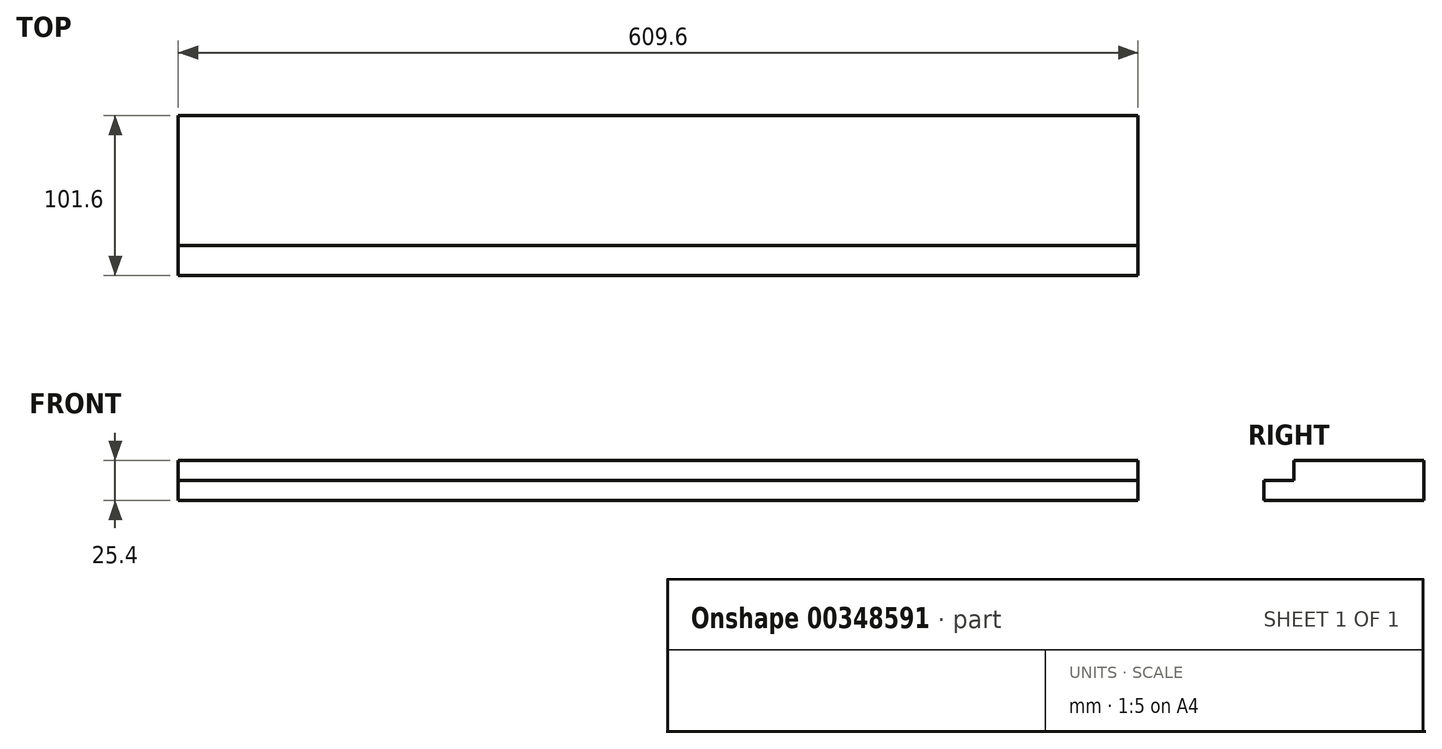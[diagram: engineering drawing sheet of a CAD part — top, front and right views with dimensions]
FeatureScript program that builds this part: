
annotation { "Feature Type Name" : "Feature", "Feature Type Description" : "" }
export const myFeature = defineFeature(function(context is Context, id is Id, definition is map)
    precondition{}
    {
        {
            var Q0;
            Q0=qCreatedBy(makeId("Top.planeOp"),FACE);
            var sketch = newSketch(context, id + "F0", { "sketchPlane" : qUnion([Q0])});
            skLineSegment(sketch, "E0.bottom", {"start": v(-308.7, 92.41) * mm, "end": v(300.9, 92.41) * mm});
            skLineSegment(sketch, "E0.top", {"start": v(-308.7, -9.19) * mm, "end": v(300.9, -9.19) * mm});
            skLineSegment(sketch, "E0.left", {"start": v(-308.7, 92.41) * mm, "end": v(-308.7, -9.19) * mm});
            skLineSegment(sketch, "E0.right", {"start": v(300.9, 92.41) * mm, "end": v(300.9, -9.19) * mm});
            skLineSegment(sketch, "E1", {"start": v(-308.7, 9.86) * mm, "end": v(300.9, 9.86) * mm});
            skSolve(sketch);
        }
        {
            var Q0;
            {var subQ0=sQuery(id+"F0.wireOp",EDGE,"E0.bottom");Q0=makeQuery(id+"F0.imprint","IMPRINT",FACE,{"disambiguationData":[TD([[makeQuery(id+"F0.imprint","IMPRINT",EDGE,{"derivedFrom":subQ0}),-1.0]])]});}
            extrude(context, id + "F1", {"entities" : qUnion([Q0]), "depth" : 12.7 * mm});
        }
        {
            var Q0;
            Q0 = qSketchRegion(id + "F0", true);
            var Q1;
            Q1=makeQuery(id+"F1.opExtrude","CAP_FACE",FACE,{"disambiguationData":[OSD([sQuery(id+"F0.wireOp",EDGE,"E0.bottom"),sQuery(id+"F0.wireOp",EDGE,"E0.left"),sQuery(id+"F0.wireOp",EDGE,"E0.right"),sQuery(id+"F0.wireOp",EDGE,"E1")])],"isStart":false});
            extrude(context, id + "F2", {"entities" : qUnion([Q0, Q1]), "operationType" : NewBodyOperationType.ADD, "depth" : 12.7 * mm});
        }
    });
